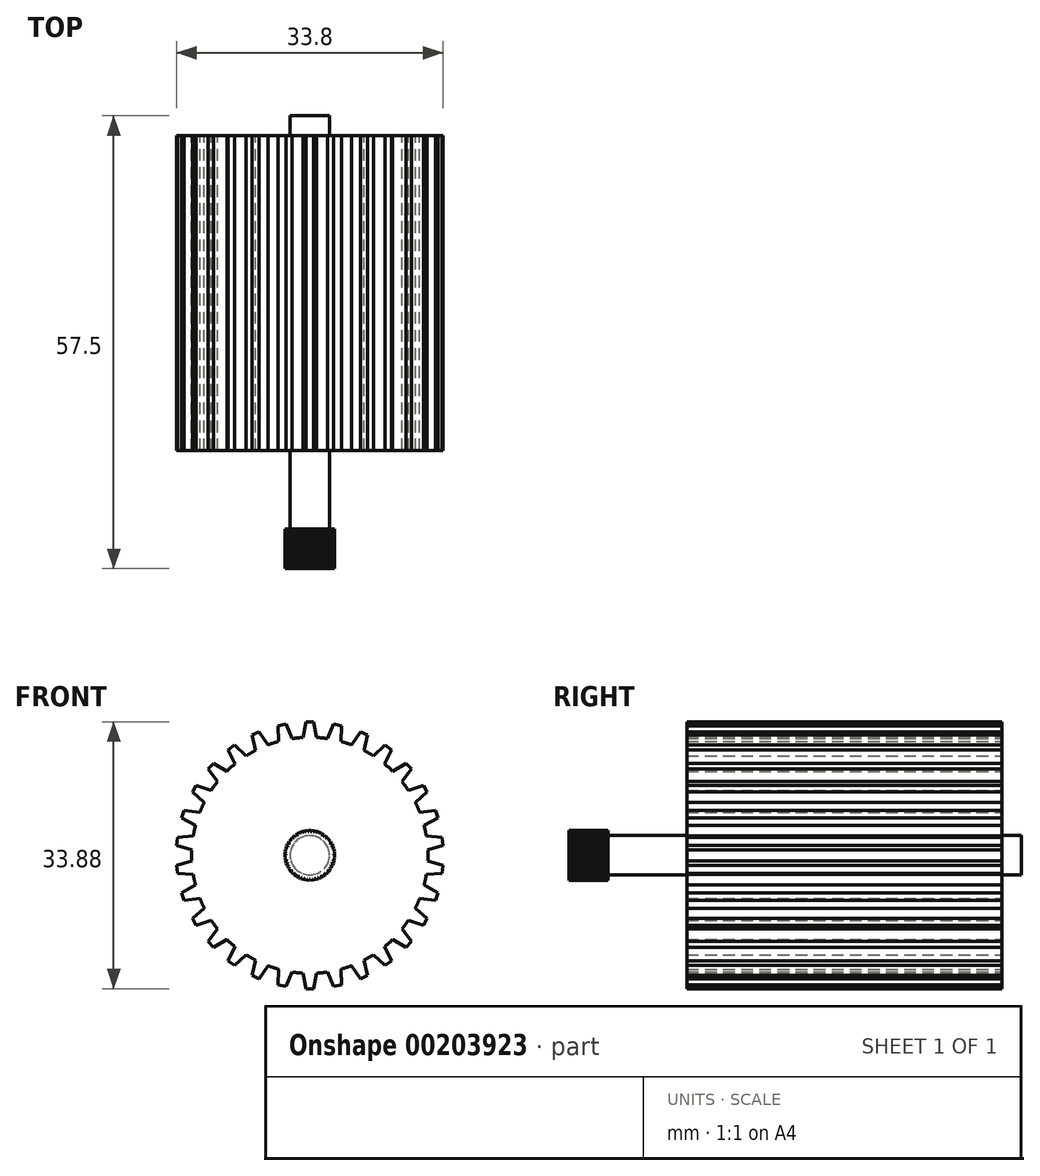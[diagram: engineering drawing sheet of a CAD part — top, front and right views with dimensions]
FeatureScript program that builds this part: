
annotation { "Feature Type Name" : "Feature", "Feature Type Description" : "" }
export const myFeature = defineFeature(function(context is Context, id is Id, definition is map)
    precondition{}
    {
        {
            var Q0;
            Q0=qCreatedBy(makeId("Front.planeOp"),FACE);
            var sketch = newSketch(context, id + "F0", { "sketchPlane" : qUnion([Q0])});
            skCircle(sketch, "E0", {"center": v(0, 0) * mm, "radius": 15 * mm});
            skLineSegment(sketch, "E1", {"start": v(0, 0) * mm, "end": v(0, 16.94) * mm, "construction": true});
            skLineSegment(sketch, "E2", {"start": v(0, 16.94) * mm, "end": v(-0.5, 16.94) * mm});
            skLineSegment(sketch, "E3", {"start": v(-0.5, 16.94) * mm, "end": v(-0.88, 14.97) * mm});
            skLineSegment(sketch, "E4.MirrorCS", {"start": v(0, 16.94) * mm, "end": v(0.5, 16.94) * mm});
            skLineSegment(sketch, "E5.MirrorCS", {"start": v(0.5, 16.94) * mm, "end": v(0.88, 14.97) * mm});
            skLineSegment(sketch, "E6.1.0", {"start": v(-4.01, 16.46) * mm, "end": v(-3.98, 14.46) * mm});
            skLineSegment(sketch, "E6.1.1", {"start": v(-3.52, 16.57) * mm, "end": v(-4.01, 16.46) * mm});
            skLineSegment(sketch, "E6.1.2", {"start": v(-3.52, 16.57) * mm, "end": v(-3.03, 16.67) * mm});
            skLineSegment(sketch, "E6.1.3", {"start": v(-3.03, 16.67) * mm, "end": v(-2.25, 14.83) * mm});
            skLineSegment(sketch, "E6.2.0", {"start": v(-7.35, 15.27) * mm, "end": v(-6.9, 13.32) * mm});
            skLineSegment(sketch, "E6.2.1", {"start": v(-6.89, 15.47) * mm, "end": v(-7.35, 15.27) * mm});
            skLineSegment(sketch, "E6.2.2", {"start": v(-6.89, 15.47) * mm, "end": v(-6.43, 15.68) * mm});
            skLineSegment(sketch, "E6.2.3", {"start": v(-6.43, 15.68) * mm, "end": v(-5.28, 14.04) * mm});
            skLineSegment(sketch, "E7.2.3.0", {"start": v(-10.36, 13.4) * mm, "end": v(-9.52, 11.6) * mm});
            skLineSegment(sketch, "E7.3.3.0", {"start": v(-9.96, 13.7) * mm, "end": v(-10.36, 13.4) * mm});
            skLineSegment(sketch, "E7.6.3.0", {"start": v(-9.96, 13.7) * mm, "end": v(-9.55, 14) * mm});
            skLineSegment(sketch, "E7.9.3.0", {"start": v(-9.55, 14) * mm, "end": v(-8.09, 12.63) * mm});
            skLineSegment(sketch, "E7.2.4.0", {"start": v(-12.92, 10.96) * mm, "end": v(-11.72, 9.36) * mm});
            skLineSegment(sketch, "E7.3.4.0", {"start": v(-12.59, 11.33) * mm, "end": v(-12.92, 10.96) * mm});
            skLineSegment(sketch, "E7.6.4.0", {"start": v(-12.59, 11.33) * mm, "end": v(-12.25, 11.7) * mm});
            skLineSegment(sketch, "E7.9.4.0", {"start": v(-12.25, 11.7) * mm, "end": v(-10.54, 10.68) * mm});
            skLineSegment(sketch, "E7.2.5.0", {"start": v(-14.92, 8.04) * mm, "end": v(-13.4, 6.72) * mm});
            skLineSegment(sketch, "E7.3.5.0", {"start": v(-14.67, 8.47) * mm, "end": v(-14.92, 8.04) * mm});
            skLineSegment(sketch, "E7.6.5.0", {"start": v(-14.67, 8.47) * mm, "end": v(-14.42, 8.9) * mm});
            skLineSegment(sketch, "E7.9.5.0", {"start": v(-14.42, 8.9) * mm, "end": v(-12.53, 8.25) * mm});
            skLineSegment(sketch, "E7.2.6.0", {"start": v(-16.26, 4.76) * mm, "end": v(-14.51, 3.79) * mm});
            skLineSegment(sketch, "E7.3.6.0", {"start": v(-16.1, 5.23) * mm, "end": v(-16.26, 4.76) * mm});
            skLineSegment(sketch, "E7.6.6.0", {"start": v(-16.1, 5.23) * mm, "end": v(-15.95, 5.7) * mm});
            skLineSegment(sketch, "E7.9.6.0", {"start": v(-15.95, 5.7) * mm, "end": v(-13.97, 5.47) * mm});
            skLineSegment(sketch, "E7.2.7.0", {"start": v(-16.9, 1.27) * mm, "end": v(-14.98, 0.69) * mm});
            skLineSegment(sketch, "E7.3.7.0", {"start": v(-16.84, 1.77) * mm, "end": v(-16.9, 1.27) * mm});
            skLineSegment(sketch, "E7.6.7.0", {"start": v(-16.84, 1.77) * mm, "end": v(-16.8, 2.27) * mm});
            skLineSegment(sketch, "E7.9.7.0", {"start": v(-16.8, 2.27) * mm, "end": v(-14.8, 2.44) * mm});
            skLineSegment(sketch, "E7.2.8.0", {"start": v(-16.8, -2.27) * mm, "end": v(-14.8, -2.44) * mm});
            skLineSegment(sketch, "E7.3.8.0", {"start": v(-16.84, -1.77) * mm, "end": v(-16.8, -2.27) * mm});
            skLineSegment(sketch, "E7.6.8.0", {"start": v(-16.84, -1.77) * mm, "end": v(-16.9, -1.27) * mm});
            skLineSegment(sketch, "E7.9.8.0", {"start": v(-16.9, -1.27) * mm, "end": v(-14.98, -0.69) * mm});
            skLineSegment(sketch, "E7.2.9.0", {"start": v(-15.95, -5.7) * mm, "end": v(-13.97, -5.47) * mm});
            skLineSegment(sketch, "E7.3.9.0", {"start": v(-16.1, -5.23) * mm, "end": v(-15.95, -5.7) * mm});
            skLineSegment(sketch, "E7.6.9.0", {"start": v(-16.1, -5.23) * mm, "end": v(-16.26, -4.76) * mm});
            skLineSegment(sketch, "E7.9.9.0", {"start": v(-16.26, -4.76) * mm, "end": v(-14.51, -3.79) * mm});
            skLineSegment(sketch, "E7.2.10.0", {"start": v(-14.42, -8.9) * mm, "end": v(-12.53, -8.25) * mm});
            skLineSegment(sketch, "E7.3.10.0", {"start": v(-14.67, -8.47) * mm, "end": v(-14.42, -8.9) * mm});
            skLineSegment(sketch, "E7.6.10.0", {"start": v(-14.67, -8.47) * mm, "end": v(-14.92, -8.04) * mm});
            skLineSegment(sketch, "E7.9.10.0", {"start": v(-14.92, -8.04) * mm, "end": v(-13.4, -6.72) * mm});
            skLineSegment(sketch, "E7.2.11.0", {"start": v(-12.25, -11.7) * mm, "end": v(-10.54, -10.68) * mm});
            skLineSegment(sketch, "E7.3.11.0", {"start": v(-12.59, -11.33) * mm, "end": v(-12.25, -11.7) * mm});
            skLineSegment(sketch, "E7.6.11.0", {"start": v(-12.59, -11.33) * mm, "end": v(-12.92, -10.96) * mm});
            skLineSegment(sketch, "E7.9.11.0", {"start": v(-12.92, -10.96) * mm, "end": v(-11.72, -9.36) * mm});
            skLineSegment(sketch, "E7.2.12.0", {"start": v(-9.55, -14) * mm, "end": v(-8.09, -12.63) * mm});
            skLineSegment(sketch, "E7.3.12.0", {"start": v(-9.96, -13.7) * mm, "end": v(-9.55, -14) * mm});
            skLineSegment(sketch, "E7.6.12.0", {"start": v(-9.96, -13.7) * mm, "end": v(-10.36, -13.4) * mm});
            skLineSegment(sketch, "E7.9.12.0", {"start": v(-10.36, -13.4) * mm, "end": v(-9.52, -11.6) * mm});
            skLineSegment(sketch, "E7.2.13.0", {"start": v(-6.43, -15.68) * mm, "end": v(-5.28, -14.04) * mm});
            skLineSegment(sketch, "E7.3.13.0", {"start": v(-6.89, -15.47) * mm, "end": v(-6.43, -15.68) * mm});
            skLineSegment(sketch, "E7.6.13.0", {"start": v(-6.89, -15.47) * mm, "end": v(-7.35, -15.27) * mm});
            skLineSegment(sketch, "E7.9.13.0", {"start": v(-7.35, -15.27) * mm, "end": v(-6.9, -13.32) * mm});
            skLineSegment(sketch, "E7.2.14.0", {"start": v(-3.03, -16.67) * mm, "end": v(-2.25, -14.83) * mm});
            skLineSegment(sketch, "E7.3.14.0", {"start": v(-3.52, -16.57) * mm, "end": v(-3.03, -16.67) * mm});
            skLineSegment(sketch, "E7.6.14.0", {"start": v(-3.52, -16.57) * mm, "end": v(-4.01, -16.46) * mm});
            skLineSegment(sketch, "E7.9.14.0", {"start": v(-4.01, -16.46) * mm, "end": v(-3.98, -14.46) * mm});
            skLineSegment(sketch, "E8.2.15.0", {"start": v(0.5, -16.94) * mm, "end": v(0.88, -14.97) * mm});
            skLineSegment(sketch, "E8.3.15.0", {"start": v(0, -16.94) * mm, "end": v(0.5, -16.94) * mm});
            skLineSegment(sketch, "E8.6.15.0", {"start": v(0, -16.94) * mm, "end": v(-0.5, -16.94) * mm});
            skLineSegment(sketch, "E8.9.15.0", {"start": v(-0.5, -16.94) * mm, "end": v(-0.88, -14.97) * mm});
            skLineSegment(sketch, "E8.2.16.0", {"start": v(4.01, -16.46) * mm, "end": v(3.98, -14.46) * mm});
            skLineSegment(sketch, "E8.3.16.0", {"start": v(3.52, -16.57) * mm, "end": v(4.01, -16.46) * mm});
            skLineSegment(sketch, "E8.6.16.0", {"start": v(3.52, -16.57) * mm, "end": v(3.03, -16.67) * mm});
            skLineSegment(sketch, "E8.9.16.0", {"start": v(3.03, -16.67) * mm, "end": v(2.25, -14.83) * mm});
            skLineSegment(sketch, "E8.2.17.0", {"start": v(7.35, -15.27) * mm, "end": v(6.9, -13.32) * mm});
            skLineSegment(sketch, "E8.3.17.0", {"start": v(6.89, -15.47) * mm, "end": v(7.35, -15.27) * mm});
            skLineSegment(sketch, "E8.6.17.0", {"start": v(6.89, -15.47) * mm, "end": v(6.43, -15.68) * mm});
            skLineSegment(sketch, "E8.9.17.0", {"start": v(6.43, -15.68) * mm, "end": v(5.28, -14.04) * mm});
            skLineSegment(sketch, "E8.2.18.0", {"start": v(10.36, -13.4) * mm, "end": v(9.52, -11.6) * mm});
            skLineSegment(sketch, "E8.3.18.0", {"start": v(9.96, -13.7) * mm, "end": v(10.36, -13.4) * mm});
            skLineSegment(sketch, "E8.6.18.0", {"start": v(9.96, -13.7) * mm, "end": v(9.55, -14) * mm});
            skLineSegment(sketch, "E8.9.18.0", {"start": v(9.55, -14) * mm, "end": v(8.09, -12.63) * mm});
            skLineSegment(sketch, "E8.2.19.0", {"start": v(12.92, -10.96) * mm, "end": v(11.72, -9.36) * mm});
            skLineSegment(sketch, "E8.3.19.0", {"start": v(12.59, -11.33) * mm, "end": v(12.92, -10.96) * mm});
            skLineSegment(sketch, "E8.6.19.0", {"start": v(12.59, -11.33) * mm, "end": v(12.25, -11.7) * mm});
            skLineSegment(sketch, "E8.9.19.0", {"start": v(12.25, -11.7) * mm, "end": v(10.54, -10.68) * mm});
            skLineSegment(sketch, "E8.2.20.0", {"start": v(14.92, -8.04) * mm, "end": v(13.4, -6.72) * mm});
            skLineSegment(sketch, "E8.3.20.0", {"start": v(14.67, -8.47) * mm, "end": v(14.92, -8.04) * mm});
            skLineSegment(sketch, "E8.6.20.0", {"start": v(14.67, -8.47) * mm, "end": v(14.42, -8.9) * mm});
            skLineSegment(sketch, "E8.9.20.0", {"start": v(14.42, -8.9) * mm, "end": v(12.53, -8.25) * mm});
            skLineSegment(sketch, "E8.2.21.0", {"start": v(16.26, -4.76) * mm, "end": v(14.51, -3.79) * mm});
            skLineSegment(sketch, "E8.3.21.0", {"start": v(16.1, -5.23) * mm, "end": v(16.26, -4.76) * mm});
            skLineSegment(sketch, "E8.6.21.0", {"start": v(16.1, -5.23) * mm, "end": v(15.95, -5.7) * mm});
            skLineSegment(sketch, "E8.9.21.0", {"start": v(15.95, -5.7) * mm, "end": v(13.97, -5.47) * mm});
            skLineSegment(sketch, "E8.2.22.0", {"start": v(16.9, -1.27) * mm, "end": v(14.98, -0.69) * mm});
            skLineSegment(sketch, "E8.3.22.0", {"start": v(16.84, -1.77) * mm, "end": v(16.9, -1.27) * mm});
            skLineSegment(sketch, "E8.6.22.0", {"start": v(16.84, -1.77) * mm, "end": v(16.8, -2.27) * mm});
            skLineSegment(sketch, "E8.9.22.0", {"start": v(16.8, -2.27) * mm, "end": v(14.8, -2.44) * mm});
            skLineSegment(sketch, "E8.2.23.0", {"start": v(16.8, 2.27) * mm, "end": v(14.8, 2.44) * mm});
            skLineSegment(sketch, "E8.3.23.0", {"start": v(16.84, 1.77) * mm, "end": v(16.8, 2.27) * mm});
            skLineSegment(sketch, "E8.6.23.0", {"start": v(16.84, 1.77) * mm, "end": v(16.9, 1.27) * mm});
            skLineSegment(sketch, "E8.9.23.0", {"start": v(16.9, 1.27) * mm, "end": v(14.98, 0.69) * mm});
            skLineSegment(sketch, "E8.2.24.0", {"start": v(15.95, 5.7) * mm, "end": v(13.97, 5.47) * mm});
            skLineSegment(sketch, "E8.3.24.0", {"start": v(16.1, 5.23) * mm, "end": v(15.95, 5.7) * mm});
            skLineSegment(sketch, "E8.6.24.0", {"start": v(16.1, 5.23) * mm, "end": v(16.26, 4.76) * mm});
            skLineSegment(sketch, "E8.9.24.0", {"start": v(16.26, 4.76) * mm, "end": v(14.51, 3.79) * mm});
            skLineSegment(sketch, "E9.2.25.0", {"start": v(14.42, 8.9) * mm, "end": v(12.53, 8.25) * mm});
            skLineSegment(sketch, "E9.3.25.0", {"start": v(14.67, 8.47) * mm, "end": v(14.42, 8.9) * mm});
            skLineSegment(sketch, "E9.6.25.0", {"start": v(14.67, 8.47) * mm, "end": v(14.92, 8.04) * mm});
            skLineSegment(sketch, "E9.9.25.0", {"start": v(14.92, 8.04) * mm, "end": v(13.4, 6.72) * mm});
            skLineSegment(sketch, "E9.2.26.0", {"start": v(12.25, 11.7) * mm, "end": v(10.54, 10.68) * mm});
            skLineSegment(sketch, "E9.3.26.0", {"start": v(12.59, 11.33) * mm, "end": v(12.25, 11.7) * mm});
            skLineSegment(sketch, "E9.6.26.0", {"start": v(12.59, 11.33) * mm, "end": v(12.92, 10.96) * mm});
            skLineSegment(sketch, "E9.9.26.0", {"start": v(12.92, 10.96) * mm, "end": v(11.72, 9.36) * mm});
            skLineSegment(sketch, "E9.2.27.0", {"start": v(9.55, 14) * mm, "end": v(8.09, 12.63) * mm});
            skLineSegment(sketch, "E9.3.27.0", {"start": v(9.96, 13.7) * mm, "end": v(9.55, 14) * mm});
            skLineSegment(sketch, "E9.6.27.0", {"start": v(9.96, 13.7) * mm, "end": v(10.36, 13.4) * mm});
            skLineSegment(sketch, "E9.9.27.0", {"start": v(10.36, 13.4) * mm, "end": v(9.52, 11.6) * mm});
            skLineSegment(sketch, "E9.2.28.0", {"start": v(6.43, 15.68) * mm, "end": v(5.28, 14.04) * mm});
            skLineSegment(sketch, "E9.3.28.0", {"start": v(6.89, 15.47) * mm, "end": v(6.43, 15.68) * mm});
            skLineSegment(sketch, "E9.6.28.0", {"start": v(6.89, 15.47) * mm, "end": v(7.35, 15.27) * mm});
            skLineSegment(sketch, "E9.9.28.0", {"start": v(7.35, 15.27) * mm, "end": v(6.9, 13.32) * mm});
            skLineSegment(sketch, "E9.2.29.0", {"start": v(3.03, 16.67) * mm, "end": v(2.25, 14.83) * mm});
            skLineSegment(sketch, "E9.3.29.0", {"start": v(3.52, 16.57) * mm, "end": v(3.03, 16.67) * mm});
            skLineSegment(sketch, "E9.6.29.0", {"start": v(3.52, 16.57) * mm, "end": v(4.01, 16.46) * mm});
            skLineSegment(sketch, "E9.9.29.0", {"start": v(4.01, 16.46) * mm, "end": v(3.98, 14.46) * mm});
            skSolve(sketch);
        }
        {
            var Q0;
            Q0=qSketchRegion(id+"F0",true);
            extrude(context, id + "F1", {"entities" : qUnion([Q0]), "depth" : 40 * mm});
        }
        {
            var Q0;
            Q0=makeQuery(id+"F1.opExtrude","CAP_FACE",FACE,{"disambiguationData":[OSD([sQuery(id+"F0.wireOp",EDGE,"E0"),sQuery(id+"F0.wireOp",EDGE,"E2"),sQuery(id+"F0.wireOp",EDGE,"E3"),sQuery(id+"F0.wireOp",EDGE,"E4.MirrorCS"),sQuery(id+"F0.wireOp",EDGE,"E5.MirrorCS"),sQuery(id+"F0.wireOp",EDGE,"E6.1.0"),sQuery(id+"F0.wireOp",EDGE,"E6.1.1"),sQuery(id+"F0.wireOp",EDGE,"E6.1.2"),sQuery(id+"F0.wireOp",EDGE,"E6.1.3"),sQuery(id+"F0.wireOp",EDGE,"E6.2.0"),sQuery(id+"F0.wireOp",EDGE,"E6.2.1"),sQuery(id+"F0.wireOp",EDGE,"E6.2.2"),sQuery(id+"F0.wireOp",EDGE,"E6.2.3"),sQuery(id+"F0.wireOp",EDGE,"E7.2.3.0"),sQuery(id+"F0.wireOp",EDGE,"E7.3.3.0"),sQuery(id+"F0.wireOp",EDGE,"E7.6.3.0"),sQuery(id+"F0.wireOp",EDGE,"E7.9.3.0"),sQuery(id+"F0.wireOp",EDGE,"E7.2.4.0"),sQuery(id+"F0.wireOp",EDGE,"E7.3.4.0"),sQuery(id+"F0.wireOp",EDGE,"E7.6.4.0"),sQuery(id+"F0.wireOp",EDGE,"E7.9.4.0"),sQuery(id+"F0.wireOp",EDGE,"E7.2.5.0"),sQuery(id+"F0.wireOp",EDGE,"E7.3.5.0"),sQuery(id+"F0.wireOp",EDGE,"E7.6.5.0"),sQuery(id+"F0.wireOp",EDGE,"E7.9.5.0"),sQuery(id+"F0.wireOp",EDGE,"E7.2.6.0"),sQuery(id+"F0.wireOp",EDGE,"E7.3.6.0"),sQuery(id+"F0.wireOp",EDGE,"E7.6.6.0"),sQuery(id+"F0.wireOp",EDGE,"E7.9.6.0"),sQuery(id+"F0.wireOp",EDGE,"E7.2.7.0"),sQuery(id+"F0.wireOp",EDGE,"E7.3.7.0"),sQuery(id+"F0.wireOp",EDGE,"E7.6.7.0"),sQuery(id+"F0.wireOp",EDGE,"E7.9.7.0"),sQuery(id+"F0.wireOp",EDGE,"E7.2.8.0"),sQuery(id+"F0.wireOp",EDGE,"E7.3.8.0"),sQuery(id+"F0.wireOp",EDGE,"E7.6.8.0"),sQuery(id+"F0.wireOp",EDGE,"E7.9.8.0"),sQuery(id+"F0.wireOp",EDGE,"E7.2.9.0"),sQuery(id+"F0.wireOp",EDGE,"E7.3.9.0"),sQuery(id+"F0.wireOp",EDGE,"E7.6.9.0"),sQuery(id+"F0.wireOp",EDGE,"E7.9.9.0"),sQuery(id+"F0.wireOp",EDGE,"E7.2.10.0"),sQuery(id+"F0.wireOp",EDGE,"E7.3.10.0"),sQuery(id+"F0.wireOp",EDGE,"E7.6.10.0"),sQuery(id+"F0.wireOp",EDGE,"E7.9.10.0"),sQuery(id+"F0.wireOp",EDGE,"E7.2.11.0"),sQuery(id+"F0.wireOp",EDGE,"E7.3.11.0"),sQuery(id+"F0.wireOp",EDGE,"E7.6.11.0"),sQuery(id+"F0.wireOp",EDGE,"E7.9.11.0"),sQuery(id+"F0.wireOp",EDGE,"E7.2.12.0"),sQuery(id+"F0.wireOp",EDGE,"E7.3.12.0"),sQuery(id+"F0.wireOp",EDGE,"E7.6.12.0"),sQuery(id+"F0.wireOp",EDGE,"E7.9.12.0"),sQuery(id+"F0.wireOp",EDGE,"E7.2.13.0"),sQuery(id+"F0.wireOp",EDGE,"E7.3.13.0"),sQuery(id+"F0.wireOp",EDGE,"E7.6.13.0"),sQuery(id+"F0.wireOp",EDGE,"E7.9.13.0"),sQuery(id+"F0.wireOp",EDGE,"E7.2.14.0"),sQuery(id+"F0.wireOp",EDGE,"E7.3.14.0"),sQuery(id+"F0.wireOp",EDGE,"E7.6.14.0"),sQuery(id+"F0.wireOp",EDGE,"E7.9.14.0"),sQuery(id+"F0.wireOp",EDGE,"E8.2.15.0"),sQuery(id+"F0.wireOp",EDGE,"E8.3.15.0"),sQuery(id+"F0.wireOp",EDGE,"E8.6.15.0"),sQuery(id+"F0.wireOp",EDGE,"E8.9.15.0"),sQuery(id+"F0.wireOp",EDGE,"E8.2.16.0"),sQuery(id+"F0.wireOp",EDGE,"E8.3.16.0"),sQuery(id+"F0.wireOp",EDGE,"E8.6.16.0"),sQuery(id+"F0.wireOp",EDGE,"E8.9.16.0"),sQuery(id+"F0.wireOp",EDGE,"E8.2.17.0"),sQuery(id+"F0.wireOp",EDGE,"E8.3.17.0"),sQuery(id+"F0.wireOp",EDGE,"E8.6.17.0"),sQuery(id+"F0.wireOp",EDGE,"E8.9.17.0"),sQuery(id+"F0.wireOp",EDGE,"E8.2.18.0"),sQuery(id+"F0.wireOp",EDGE,"E8.3.18.0"),sQuery(id+"F0.wireOp",EDGE,"E8.6.18.0"),sQuery(id+"F0.wireOp",EDGE,"E8.9.18.0"),sQuery(id+"F0.wireOp",EDGE,"E8.2.19.0"),sQuery(id+"F0.wireOp",EDGE,"E8.3.19.0"),sQuery(id+"F0.wireOp",EDGE,"E8.6.19.0"),sQuery(id+"F0.wireOp",EDGE,"E8.9.19.0"),sQuery(id+"F0.wireOp",EDGE,"E8.2.20.0"),sQuery(id+"F0.wireOp",EDGE,"E8.3.20.0"),sQuery(id+"F0.wireOp",EDGE,"E8.6.20.0"),sQuery(id+"F0.wireOp",EDGE,"E8.9.20.0"),sQuery(id+"F0.wireOp",EDGE,"E8.2.21.0"),sQuery(id+"F0.wireOp",EDGE,"E8.3.21.0"),sQuery(id+"F0.wireOp",EDGE,"E8.6.21.0"),sQuery(id+"F0.wireOp",EDGE,"E8.9.21.0"),sQuery(id+"F0.wireOp",EDGE,"E8.2.22.0"),sQuery(id+"F0.wireOp",EDGE,"E8.3.22.0"),sQuery(id+"F0.wireOp",EDGE,"E8.6.22.0"),sQuery(id+"F0.wireOp",EDGE,"E8.9.22.0"),sQuery(id+"F0.wireOp",EDGE,"E8.2.23.0"),sQuery(id+"F0.wireOp",EDGE,"E8.3.23.0"),sQuery(id+"F0.wireOp",EDGE,"E8.6.23.0"),sQuery(id+"F0.wireOp",EDGE,"E8.9.23.0"),sQuery(id+"F0.wireOp",EDGE,"E8.2.24.0"),sQuery(id+"F0.wireOp",EDGE,"E8.3.24.0"),sQuery(id+"F0.wireOp",EDGE,"E8.6.24.0"),sQuery(id+"F0.wireOp",EDGE,"E8.9.24.0"),sQuery(id+"F0.wireOp",EDGE,"E9.2.25.0"),sQuery(id+"F0.wireOp",EDGE,"E9.3.25.0"),sQuery(id+"F0.wireOp",EDGE,"E9.6.25.0"),sQuery(id+"F0.wireOp",EDGE,"E9.9.25.0"),sQuery(id+"F0.wireOp",EDGE,"E9.2.26.0"),sQuery(id+"F0.wireOp",EDGE,"E9.3.26.0"),sQuery(id+"F0.wireOp",EDGE,"E9.6.26.0"),sQuery(id+"F0.wireOp",EDGE,"E9.9.26.0"),sQuery(id+"F0.wireOp",EDGE,"E9.2.27.0"),sQuery(id+"F0.wireOp",EDGE,"E9.3.27.0"),sQuery(id+"F0.wireOp",EDGE,"E9.6.27.0"),sQuery(id+"F0.wireOp",EDGE,"E9.9.27.0"),sQuery(id+"F0.wireOp",EDGE,"E9.2.28.0"),sQuery(id+"F0.wireOp",EDGE,"E9.3.28.0"),sQuery(id+"F0.wireOp",EDGE,"E9.6.28.0"),sQuery(id+"F0.wireOp",EDGE,"E9.9.28.0"),sQuery(id+"F0.wireOp",EDGE,"E9.2.29.0"),sQuery(id+"F0.wireOp",EDGE,"E9.3.29.0"),sQuery(id+"F0.wireOp",EDGE,"E9.6.29.0"),sQuery(id+"F0.wireOp",EDGE,"E9.9.29.0")])],"isStart":false});
            var sketch = newSketch(context, id + "F2", { "sketchPlane" : qUnion([Q0])});
            skCircle(sketch, "E10", {"center": v(0, 0) * mm, "radius": 2.5 * mm});
            skSolve(sketch);
        }
        {
            var Q0;
            Q0=qSketchRegion(id+"F2",true);
            extrude(context, id + "F3", {"entities" : qUnion([Q0]), "operationType" : NewBodyOperationType.ADD, "depth" : 15 * mm});
        }
        {
            var Q0;
            Q0=makeQuery(id+"F1.opExtrude","CAP_FACE",FACE,{"disambiguationData":[OSD([sQuery(id+"F0.wireOp",EDGE,"E0"),sQuery(id+"F0.wireOp",EDGE,"E2"),sQuery(id+"F0.wireOp",EDGE,"E3"),sQuery(id+"F0.wireOp",EDGE,"E4.MirrorCS"),sQuery(id+"F0.wireOp",EDGE,"E5.MirrorCS"),sQuery(id+"F0.wireOp",EDGE,"E6.1.0"),sQuery(id+"F0.wireOp",EDGE,"E6.1.1"),sQuery(id+"F0.wireOp",EDGE,"E6.1.2"),sQuery(id+"F0.wireOp",EDGE,"E6.1.3"),sQuery(id+"F0.wireOp",EDGE,"E6.2.0"),sQuery(id+"F0.wireOp",EDGE,"E6.2.1"),sQuery(id+"F0.wireOp",EDGE,"E6.2.2"),sQuery(id+"F0.wireOp",EDGE,"E6.2.3"),sQuery(id+"F0.wireOp",EDGE,"E7.2.3.0"),sQuery(id+"F0.wireOp",EDGE,"E7.3.3.0"),sQuery(id+"F0.wireOp",EDGE,"E7.6.3.0"),sQuery(id+"F0.wireOp",EDGE,"E7.9.3.0"),sQuery(id+"F0.wireOp",EDGE,"E7.2.4.0"),sQuery(id+"F0.wireOp",EDGE,"E7.3.4.0"),sQuery(id+"F0.wireOp",EDGE,"E7.6.4.0"),sQuery(id+"F0.wireOp",EDGE,"E7.9.4.0"),sQuery(id+"F0.wireOp",EDGE,"E7.2.5.0"),sQuery(id+"F0.wireOp",EDGE,"E7.3.5.0"),sQuery(id+"F0.wireOp",EDGE,"E7.6.5.0"),sQuery(id+"F0.wireOp",EDGE,"E7.9.5.0"),sQuery(id+"F0.wireOp",EDGE,"E7.2.6.0"),sQuery(id+"F0.wireOp",EDGE,"E7.3.6.0"),sQuery(id+"F0.wireOp",EDGE,"E7.6.6.0"),sQuery(id+"F0.wireOp",EDGE,"E7.9.6.0"),sQuery(id+"F0.wireOp",EDGE,"E7.2.7.0"),sQuery(id+"F0.wireOp",EDGE,"E7.3.7.0"),sQuery(id+"F0.wireOp",EDGE,"E7.6.7.0"),sQuery(id+"F0.wireOp",EDGE,"E7.9.7.0"),sQuery(id+"F0.wireOp",EDGE,"E7.2.8.0"),sQuery(id+"F0.wireOp",EDGE,"E7.3.8.0"),sQuery(id+"F0.wireOp",EDGE,"E7.6.8.0"),sQuery(id+"F0.wireOp",EDGE,"E7.9.8.0"),sQuery(id+"F0.wireOp",EDGE,"E7.2.9.0"),sQuery(id+"F0.wireOp",EDGE,"E7.3.9.0"),sQuery(id+"F0.wireOp",EDGE,"E7.6.9.0"),sQuery(id+"F0.wireOp",EDGE,"E7.9.9.0"),sQuery(id+"F0.wireOp",EDGE,"E7.2.10.0"),sQuery(id+"F0.wireOp",EDGE,"E7.3.10.0"),sQuery(id+"F0.wireOp",EDGE,"E7.6.10.0"),sQuery(id+"F0.wireOp",EDGE,"E7.9.10.0"),sQuery(id+"F0.wireOp",EDGE,"E7.2.11.0"),sQuery(id+"F0.wireOp",EDGE,"E7.3.11.0"),sQuery(id+"F0.wireOp",EDGE,"E7.6.11.0"),sQuery(id+"F0.wireOp",EDGE,"E7.9.11.0"),sQuery(id+"F0.wireOp",EDGE,"E7.2.12.0"),sQuery(id+"F0.wireOp",EDGE,"E7.3.12.0"),sQuery(id+"F0.wireOp",EDGE,"E7.6.12.0"),sQuery(id+"F0.wireOp",EDGE,"E7.9.12.0"),sQuery(id+"F0.wireOp",EDGE,"E7.2.13.0"),sQuery(id+"F0.wireOp",EDGE,"E7.3.13.0"),sQuery(id+"F0.wireOp",EDGE,"E7.6.13.0"),sQuery(id+"F0.wireOp",EDGE,"E7.9.13.0"),sQuery(id+"F0.wireOp",EDGE,"E7.2.14.0"),sQuery(id+"F0.wireOp",EDGE,"E7.3.14.0"),sQuery(id+"F0.wireOp",EDGE,"E7.6.14.0"),sQuery(id+"F0.wireOp",EDGE,"E7.9.14.0"),sQuery(id+"F0.wireOp",EDGE,"E8.2.15.0"),sQuery(id+"F0.wireOp",EDGE,"E8.3.15.0"),sQuery(id+"F0.wireOp",EDGE,"E8.6.15.0"),sQuery(id+"F0.wireOp",EDGE,"E8.9.15.0"),sQuery(id+"F0.wireOp",EDGE,"E8.2.16.0"),sQuery(id+"F0.wireOp",EDGE,"E8.3.16.0"),sQuery(id+"F0.wireOp",EDGE,"E8.6.16.0"),sQuery(id+"F0.wireOp",EDGE,"E8.9.16.0"),sQuery(id+"F0.wireOp",EDGE,"E8.2.17.0"),sQuery(id+"F0.wireOp",EDGE,"E8.3.17.0"),sQuery(id+"F0.wireOp",EDGE,"E8.6.17.0"),sQuery(id+"F0.wireOp",EDGE,"E8.9.17.0"),sQuery(id+"F0.wireOp",EDGE,"E8.2.18.0"),sQuery(id+"F0.wireOp",EDGE,"E8.3.18.0"),sQuery(id+"F0.wireOp",EDGE,"E8.6.18.0"),sQuery(id+"F0.wireOp",EDGE,"E8.9.18.0"),sQuery(id+"F0.wireOp",EDGE,"E8.2.19.0"),sQuery(id+"F0.wireOp",EDGE,"E8.3.19.0"),sQuery(id+"F0.wireOp",EDGE,"E8.6.19.0"),sQuery(id+"F0.wireOp",EDGE,"E8.9.19.0"),sQuery(id+"F0.wireOp",EDGE,"E8.2.20.0"),sQuery(id+"F0.wireOp",EDGE,"E8.3.20.0"),sQuery(id+"F0.wireOp",EDGE,"E8.6.20.0"),sQuery(id+"F0.wireOp",EDGE,"E8.9.20.0"),sQuery(id+"F0.wireOp",EDGE,"E8.2.21.0"),sQuery(id+"F0.wireOp",EDGE,"E8.3.21.0"),sQuery(id+"F0.wireOp",EDGE,"E8.6.21.0"),sQuery(id+"F0.wireOp",EDGE,"E8.9.21.0"),sQuery(id+"F0.wireOp",EDGE,"E8.2.22.0"),sQuery(id+"F0.wireOp",EDGE,"E8.3.22.0"),sQuery(id+"F0.wireOp",EDGE,"E8.6.22.0"),sQuery(id+"F0.wireOp",EDGE,"E8.9.22.0"),sQuery(id+"F0.wireOp",EDGE,"E8.2.23.0"),sQuery(id+"F0.wireOp",EDGE,"E8.3.23.0"),sQuery(id+"F0.wireOp",EDGE,"E8.6.23.0"),sQuery(id+"F0.wireOp",EDGE,"E8.9.23.0"),sQuery(id+"F0.wireOp",EDGE,"E8.2.24.0"),sQuery(id+"F0.wireOp",EDGE,"E8.3.24.0"),sQuery(id+"F0.wireOp",EDGE,"E8.6.24.0"),sQuery(id+"F0.wireOp",EDGE,"E8.9.24.0"),sQuery(id+"F0.wireOp",EDGE,"E9.2.25.0"),sQuery(id+"F0.wireOp",EDGE,"E9.3.25.0"),sQuery(id+"F0.wireOp",EDGE,"E9.6.25.0"),sQuery(id+"F0.wireOp",EDGE,"E9.9.25.0"),sQuery(id+"F0.wireOp",EDGE,"E9.2.26.0"),sQuery(id+"F0.wireOp",EDGE,"E9.3.26.0"),sQuery(id+"F0.wireOp",EDGE,"E9.6.26.0"),sQuery(id+"F0.wireOp",EDGE,"E9.9.26.0"),sQuery(id+"F0.wireOp",EDGE,"E9.2.27.0"),sQuery(id+"F0.wireOp",EDGE,"E9.3.27.0"),sQuery(id+"F0.wireOp",EDGE,"E9.6.27.0"),sQuery(id+"F0.wireOp",EDGE,"E9.9.27.0"),sQuery(id+"F0.wireOp",EDGE,"E9.2.28.0"),sQuery(id+"F0.wireOp",EDGE,"E9.3.28.0"),sQuery(id+"F0.wireOp",EDGE,"E9.6.28.0"),sQuery(id+"F0.wireOp",EDGE,"E9.9.28.0"),sQuery(id+"F0.wireOp",EDGE,"E9.2.29.0"),sQuery(id+"F0.wireOp",EDGE,"E9.3.29.0"),sQuery(id+"F0.wireOp",EDGE,"E9.6.29.0"),sQuery(id+"F0.wireOp",EDGE,"E9.9.29.0")])],"isStart":true});
            var sketch = newSketch(context, id + "F4", { "sketchPlane" : qUnion([Q0])});
            skCircle(sketch, "E11", {"center": v(0, 0) * mm, "radius": 2.5 * mm});
            skSolve(sketch);
        }
        {
            var Q0;
            Q0=qSketchRegion(id+"F4",true);
            extrude(context, id + "F5", {"entities" : qUnion([Q0]), "operationType" : NewBodyOperationType.ADD, "depth" : 2.5 * mm});
        }
        {
            var Q0;
            Q0=makeQuery(id+"F3.opExtrude","CAP_FACE",FACE,{"disambiguationData":[OSD([sQuery(id+"F2.wireOp",EDGE,"E10")])],"isStart":false});
            var sketch = newSketch(context, id + "F6", { "sketchPlane" : qUnion([Q0])});
            skCircle(sketch, "E12", {"center": v(0, 0) * mm, "radius": 3 * mm});
            skLineSegment(sketch, "E13", {"start": v(0, 0) * mm, "end": v(0, 5.06) * mm, "construction": true});
            skLineSegment(sketch, "E14.bottom", {"start": v(0.15, 3.15) * mm, "end": v(-0.15, 3.15) * mm});
            skLineSegment(sketch, "E14.top", {"start": v(0.15, 2.85) * mm, "end": v(-0.15, 2.85) * mm});
            skLineSegment(sketch, "E14.left", {"start": v(0.15, 3.15) * mm, "end": v(0.15, 2.85) * mm});
            skLineSegment(sketch, "E14.right", {"start": v(-0.15, 3.15) * mm, "end": v(-0.15, 2.85) * mm});
            skPoint(sketch, "E14.middle", {"position": v(0, 3) * mm});
            skLineSegment(sketch, "E15.1.0", {"start": v(-0.21, 3.15) * mm, "end": v(-0.18, 2.85) * mm});
            skLineSegment(sketch, "E15.1.1", {"start": v(-0.21, 3.15) * mm, "end": v(-0.5, 3.11) * mm});
            skLineSegment(sketch, "E15.1.2", {"start": v(-0.5, 3.11) * mm, "end": v(-0.47, 2.81) * mm});
            skLineSegment(sketch, "E15.1.3", {"start": v(-0.18, 2.85) * mm, "end": v(-0.47, 2.81) * mm});
            skLineSegment(sketch, "E15.2.0", {"start": v(-0.57, 3.1) * mm, "end": v(-0.5, 2.8) * mm});
            skLineSegment(sketch, "E15.2.1", {"start": v(-0.57, 3.1) * mm, "end": v(-0.86, 3.03) * mm});
            skLineSegment(sketch, "E15.2.2", {"start": v(-0.86, 3.03) * mm, "end": v(-0.8, 2.74) * mm});
            skLineSegment(sketch, "E15.2.3", {"start": v(-0.5, 2.8) * mm, "end": v(-0.8, 2.74) * mm});
            skLineSegment(sketch, "E16.2.3.0", {"start": v(-0.92, 3.02) * mm, "end": v(-0.82, 2.73) * mm});
            skLineSegment(sketch, "E16.3.3.0", {"start": v(-0.92, 3.02) * mm, "end": v(-1.2, 2.92) * mm});
            skLineSegment(sketch, "E16.6.3.0", {"start": v(-1.2, 2.92) * mm, "end": v(-1.1, 2.63) * mm});
            skLineSegment(sketch, "E16.9.3.0", {"start": v(-0.82, 2.73) * mm, "end": v(-1.1, 2.63) * mm});
            skLineSegment(sketch, "E16.2.4.0", {"start": v(-1.26, 2.9) * mm, "end": v(-1.12, 2.62) * mm});
            skLineSegment(sketch, "E16.3.4.0", {"start": v(-1.26, 2.9) * mm, "end": v(-1.52, 2.76) * mm});
            skLineSegment(sketch, "E16.6.4.0", {"start": v(-1.52, 2.76) * mm, "end": v(-1.4, 2.5) * mm});
            skLineSegment(sketch, "E16.9.4.0", {"start": v(-1.12, 2.62) * mm, "end": v(-1.4, 2.5) * mm});
            skLineSegment(sketch, "E16.2.5.0", {"start": v(-1.58, 2.73) * mm, "end": v(-1.41, 2.48) * mm});
            skLineSegment(sketch, "E16.3.5.0", {"start": v(-1.58, 2.73) * mm, "end": v(-1.83, 2.57) * mm});
            skLineSegment(sketch, "E16.6.5.0", {"start": v(-1.83, 2.57) * mm, "end": v(-1.67, 2.32) * mm});
            skLineSegment(sketch, "E16.9.5.0", {"start": v(-1.41, 2.48) * mm, "end": v(-1.67, 2.32) * mm});
            skLineSegment(sketch, "E16.2.6.0", {"start": v(-1.88, 2.53) * mm, "end": v(-1.69, 2.3) * mm});
            skLineSegment(sketch, "E16.3.6.0", {"start": v(-1.88, 2.53) * mm, "end": v(-2.11, 2.34) * mm});
            skLineSegment(sketch, "E16.6.6.0", {"start": v(-2.11, 2.34) * mm, "end": v(-1.92, 2.11) * mm});
            skLineSegment(sketch, "E16.9.6.0", {"start": v(-1.69, 2.3) * mm, "end": v(-1.92, 2.11) * mm});
            skLineSegment(sketch, "E16.2.7.0", {"start": v(-2.15, 2.3) * mm, "end": v(-1.94, 2.1) * mm});
            skLineSegment(sketch, "E16.3.7.0", {"start": v(-2.15, 2.3) * mm, "end": v(-2.36, 2.09) * mm});
            skLineSegment(sketch, "E16.6.7.0", {"start": v(-2.36, 2.09) * mm, "end": v(-2.15, 1.88) * mm});
            skLineSegment(sketch, "E16.9.7.0", {"start": v(-1.94, 2.1) * mm, "end": v(-2.15, 1.88) * mm});
            skLineSegment(sketch, "E16.2.8.0", {"start": v(-2.4, 2.04) * mm, "end": v(-2.17, 1.86) * mm});
            skLineSegment(sketch, "E16.3.8.0", {"start": v(-2.4, 2.04) * mm, "end": v(-2.59, 1.8) * mm});
            skLineSegment(sketch, "E16.6.8.0", {"start": v(-2.59, 1.8) * mm, "end": v(-2.35, 1.62) * mm});
            skLineSegment(sketch, "E16.9.8.0", {"start": v(-2.17, 1.86) * mm, "end": v(-2.35, 1.62) * mm});
            skLineSegment(sketch, "E16.2.9.0", {"start": v(-2.62, 1.76) * mm, "end": v(-2.36, 1.6) * mm});
            skLineSegment(sketch, "E16.3.9.0", {"start": v(-2.62, 1.76) * mm, "end": v(-2.77, 1.5) * mm});
            skLineSegment(sketch, "E16.6.9.0", {"start": v(-2.77, 1.5) * mm, "end": v(-2.52, 1.34) * mm});
            skLineSegment(sketch, "E16.9.9.0", {"start": v(-2.36, 1.6) * mm, "end": v(-2.52, 1.34) * mm});
            skLineSegment(sketch, "E17.2.10.0", {"start": v(-2.8, 1.45) * mm, "end": v(-2.53, 1.32) * mm});
            skLineSegment(sketch, "E17.3.10.0", {"start": v(-2.8, 1.45) * mm, "end": v(-2.93, 1.17) * mm});
            skLineSegment(sketch, "E17.6.10.0", {"start": v(-2.93, 1.17) * mm, "end": v(-2.65, 1.05) * mm});
            skLineSegment(sketch, "E17.9.10.0", {"start": v(-2.53, 1.32) * mm, "end": v(-2.65, 1.05) * mm});
            skLineSegment(sketch, "E17.2.11.0", {"start": v(-2.95, 1.12) * mm, "end": v(-2.66, 1.02) * mm});
            skLineSegment(sketch, "E17.3.11.0", {"start": v(-2.95, 1.12) * mm, "end": v(-3.04, 0.83) * mm});
            skLineSegment(sketch, "E17.6.11.0", {"start": v(-3.04, 0.83) * mm, "end": v(-2.76, 0.74) * mm});
            skLineSegment(sketch, "E17.9.11.0", {"start": v(-2.66, 1.02) * mm, "end": v(-2.76, 0.74) * mm});
            skLineSegment(sketch, "E17.2.12.0", {"start": v(-3.06, 0.77) * mm, "end": v(-2.76, 0.71) * mm});
            skLineSegment(sketch, "E17.3.12.0", {"start": v(-3.06, 0.77) * mm, "end": v(-3.12, 0.48) * mm});
            skLineSegment(sketch, "E17.6.12.0", {"start": v(-3.12, 0.48) * mm, "end": v(-2.82, 0.42) * mm});
            skLineSegment(sketch, "E17.9.12.0", {"start": v(-2.76, 0.71) * mm, "end": v(-2.82, 0.42) * mm});
            skLineSegment(sketch, "E17.2.13.0", {"start": v(-3.13, 0.42) * mm, "end": v(-2.83, 0.4) * mm});
            skLineSegment(sketch, "E17.3.13.0", {"start": v(-3.13, 0.42) * mm, "end": v(-3.15, 0.12) * mm});
            skLineSegment(sketch, "E17.6.13.0", {"start": v(-3.15, 0.12) * mm, "end": v(-2.85, 0.1) * mm});
            skLineSegment(sketch, "E17.9.13.0", {"start": v(-2.83, 0.4) * mm, "end": v(-2.85, 0.1) * mm});
            skLineSegment(sketch, "E17.2.14.0", {"start": v(-3.15, 0.06) * mm, "end": v(-2.85, 0.07) * mm});
            skLineSegment(sketch, "E17.3.14.0", {"start": v(-3.15, 0.06) * mm, "end": v(-3.14, -0.24) * mm});
            skLineSegment(sketch, "E17.6.14.0", {"start": v(-3.14, -0.24) * mm, "end": v(-2.84, -0.23) * mm});
            skLineSegment(sketch, "E17.9.14.0", {"start": v(-2.85, 0.07) * mm, "end": v(-2.84, -0.23) * mm});
            skLineSegment(sketch, "E17.2.15.0", {"start": v(-3.14, -0.3) * mm, "end": v(-2.84, -0.26) * mm});
            skLineSegment(sketch, "E17.3.15.0", {"start": v(-3.14, -0.3) * mm, "end": v(-3.1, -0.6) * mm});
            skLineSegment(sketch, "E17.6.15.0", {"start": v(-3.1, -0.6) * mm, "end": v(-2.8, -0.55) * mm});
            skLineSegment(sketch, "E17.9.15.0", {"start": v(-2.84, -0.26) * mm, "end": v(-2.8, -0.55) * mm});
            skLineSegment(sketch, "E17.2.16.0", {"start": v(-3.08, -0.66) * mm, "end": v(-2.8, -0.58) * mm});
            skLineSegment(sketch, "E17.3.16.0", {"start": v(-3.08, -0.66) * mm, "end": v(-3, -0.95) * mm});
            skLineSegment(sketch, "E17.6.16.0", {"start": v(-3, -0.95) * mm, "end": v(-2.72, -0.87) * mm});
            skLineSegment(sketch, "E17.9.16.0", {"start": v(-2.8, -0.58) * mm, "end": v(-2.72, -0.87) * mm});
            skLineSegment(sketch, "E17.2.17.0", {"start": v(-2.99, -1) * mm, "end": v(-2.71, -0.9) * mm});
            skLineSegment(sketch, "E17.3.17.0", {"start": v(-2.99, -1) * mm, "end": v(-2.88, -1.28) * mm});
            skLineSegment(sketch, "E17.6.17.0", {"start": v(-2.88, -1.28) * mm, "end": v(-2.6, -1.17) * mm});
            skLineSegment(sketch, "E17.9.17.0", {"start": v(-2.71, -0.9) * mm, "end": v(-2.6, -1.17) * mm});
            skLineSegment(sketch, "E17.2.18.0", {"start": v(-2.86, -1.34) * mm, "end": v(-2.6, -1.2) * mm});
            skLineSegment(sketch, "E17.3.18.0", {"start": v(-2.86, -1.34) * mm, "end": v(-2.72, -1.6) * mm});
            skLineSegment(sketch, "E17.6.18.0", {"start": v(-2.72, -1.6) * mm, "end": v(-2.45, -1.46) * mm});
            skLineSegment(sketch, "E17.9.18.0", {"start": v(-2.6, -1.2) * mm, "end": v(-2.45, -1.46) * mm});
            skLineSegment(sketch, "E17.2.19.0", {"start": v(-2.68, -1.65) * mm, "end": v(-2.44, -1.48) * mm});
            skLineSegment(sketch, "E17.3.19.0", {"start": v(-2.68, -1.65) * mm, "end": v(-2.52, -1.9) * mm});
            skLineSegment(sketch, "E17.6.19.0", {"start": v(-2.52, -1.9) * mm, "end": v(-2.27, -1.73) * mm});
            skLineSegment(sketch, "E17.9.19.0", {"start": v(-2.44, -1.48) * mm, "end": v(-2.27, -1.73) * mm});
            skLineSegment(sketch, "E18.2.20.0", {"start": v(-2.48, -1.95) * mm, "end": v(-2.25, -1.75) * mm});
            skLineSegment(sketch, "E18.3.20.0", {"start": v(-2.48, -1.95) * mm, "end": v(-2.28, -2.18) * mm});
            skLineSegment(sketch, "E18.6.20.0", {"start": v(-2.28, -2.18) * mm, "end": v(-2.06, -1.98) * mm});
            skLineSegment(sketch, "E18.9.20.0", {"start": v(-2.25, -1.75) * mm, "end": v(-2.06, -1.98) * mm});
            skLineSegment(sketch, "E18.2.21.0", {"start": v(-2.24, -2.22) * mm, "end": v(-2.04, -2) * mm});
            skLineSegment(sketch, "E18.3.21.0", {"start": v(-2.24, -2.22) * mm, "end": v(-2.02, -2.42) * mm});
            skLineSegment(sketch, "E18.6.21.0", {"start": v(-2.02, -2.42) * mm, "end": v(-1.82, -2.2) * mm});
            skLineSegment(sketch, "E18.9.21.0", {"start": v(-2.04, -2) * mm, "end": v(-1.82, -2.2) * mm});
            skLineSegment(sketch, "E18.2.22.0", {"start": v(-1.97, -2.46) * mm, "end": v(-1.8, -2.22) * mm});
            skLineSegment(sketch, "E18.3.22.0", {"start": v(-1.97, -2.46) * mm, "end": v(-1.73, -2.64) * mm});
            skLineSegment(sketch, "E18.6.22.0", {"start": v(-1.73, -2.64) * mm, "end": v(-1.55, -2.4) * mm});
            skLineSegment(sketch, "E18.9.22.0", {"start": v(-1.8, -2.22) * mm, "end": v(-1.55, -2.4) * mm});
            skLineSegment(sketch, "E18.2.23.0", {"start": v(-1.68, -2.67) * mm, "end": v(-1.53, -2.4) * mm});
            skLineSegment(sketch, "E18.3.23.0", {"start": v(-1.68, -2.67) * mm, "end": v(-1.42, -2.82) * mm});
            skLineSegment(sketch, "E18.6.23.0", {"start": v(-1.42, -2.82) * mm, "end": v(-1.27, -2.56) * mm});
            skLineSegment(sketch, "E18.9.23.0", {"start": v(-1.53, -2.4) * mm, "end": v(-1.27, -2.56) * mm});
            skLineSegment(sketch, "E18.2.24.0", {"start": v(-1.36, -2.84) * mm, "end": v(-1.25, -2.57) * mm});
            skLineSegment(sketch, "E18.3.24.0", {"start": v(-1.36, -2.84) * mm, "end": v(-1.09, -2.96) * mm});
            skLineSegment(sketch, "E18.6.24.0", {"start": v(-1.09, -2.96) * mm, "end": v(-0.97, -2.68) * mm});
            skLineSegment(sketch, "E18.9.24.0", {"start": v(-1.25, -2.57) * mm, "end": v(-0.97, -2.68) * mm});
            skLineSegment(sketch, "E18.2.25.0", {"start": v(-1.03, -2.98) * mm, "end": v(-0.95, -2.7) * mm});
            skLineSegment(sketch, "E18.3.25.0", {"start": v(-1.03, -2.98) * mm, "end": v(-0.74, -3.06) * mm});
            skLineSegment(sketch, "E18.6.25.0", {"start": v(-0.74, -3.06) * mm, "end": v(-0.66, -2.78) * mm});
            skLineSegment(sketch, "E18.9.25.0", {"start": v(-0.95, -2.7) * mm, "end": v(-0.66, -2.78) * mm});
            skLineSegment(sketch, "E18.2.26.0", {"start": v(-0.68, -3.08) * mm, "end": v(-0.63, -2.78) * mm});
            skLineSegment(sketch, "E18.3.26.0", {"start": v(-0.68, -3.08) * mm, "end": v(-0.39, -3.13) * mm});
            skLineSegment(sketch, "E18.6.26.0", {"start": v(-0.39, -3.13) * mm, "end": v(-0.34, -2.83) * mm});
            skLineSegment(sketch, "E18.9.26.0", {"start": v(-0.63, -2.78) * mm, "end": v(-0.34, -2.83) * mm});
            skLineSegment(sketch, "E18.2.27.0", {"start": v(-0.33, -3.14) * mm, "end": v(-0.31, -2.84) * mm});
            skLineSegment(sketch, "E18.3.27.0", {"start": v(-0.33, -3.14) * mm, "end": v(-0.03, -3.15) * mm});
            skLineSegment(sketch, "E18.6.27.0", {"start": v(-0.03, -3.15) * mm, "end": v(-0.01, -2.85) * mm});
            skLineSegment(sketch, "E18.9.27.0", {"start": v(-0.31, -2.84) * mm, "end": v(-0.01, -2.85) * mm});
            skLineSegment(sketch, "E18.2.28.0", {"start": v(0.03, -3.15) * mm, "end": v(0.01, -2.85) * mm});
            skLineSegment(sketch, "E18.3.28.0", {"start": v(0.03, -3.15) * mm, "end": v(0.33, -3.14) * mm});
            skLineSegment(sketch, "E18.6.28.0", {"start": v(0.33, -3.14) * mm, "end": v(0.31, -2.84) * mm});
            skLineSegment(sketch, "E18.9.28.0", {"start": v(0.01, -2.85) * mm, "end": v(0.31, -2.84) * mm});
            skLineSegment(sketch, "E18.2.29.0", {"start": v(0.39, -3.13) * mm, "end": v(0.34, -2.83) * mm});
            skLineSegment(sketch, "E18.3.29.0", {"start": v(0.39, -3.13) * mm, "end": v(0.68, -3.08) * mm});
            skLineSegment(sketch, "E18.6.29.0", {"start": v(0.68, -3.08) * mm, "end": v(0.63, -2.78) * mm});
            skLineSegment(sketch, "E18.9.29.0", {"start": v(0.34, -2.83) * mm, "end": v(0.63, -2.78) * mm});
            skLineSegment(sketch, "E19.2.30.0", {"start": v(0.74, -3.06) * mm, "end": v(0.66, -2.78) * mm});
            skLineSegment(sketch, "E19.3.30.0", {"start": v(0.74, -3.06) * mm, "end": v(1.03, -2.98) * mm});
            skLineSegment(sketch, "E19.6.30.0", {"start": v(1.03, -2.98) * mm, "end": v(0.95, -2.7) * mm});
            skLineSegment(sketch, "E19.9.30.0", {"start": v(0.66, -2.78) * mm, "end": v(0.95, -2.7) * mm});
            skLineSegment(sketch, "E19.2.31.0", {"start": v(1.09, -2.96) * mm, "end": v(0.97, -2.68) * mm});
            skLineSegment(sketch, "E19.3.31.0", {"start": v(1.09, -2.96) * mm, "end": v(1.36, -2.84) * mm});
            skLineSegment(sketch, "E19.6.31.0", {"start": v(1.36, -2.84) * mm, "end": v(1.25, -2.57) * mm});
            skLineSegment(sketch, "E19.9.31.0", {"start": v(0.97, -2.68) * mm, "end": v(1.25, -2.57) * mm});
            skLineSegment(sketch, "E19.2.32.0", {"start": v(1.42, -2.82) * mm, "end": v(1.27, -2.56) * mm});
            skLineSegment(sketch, "E19.3.32.0", {"start": v(1.42, -2.82) * mm, "end": v(1.68, -2.67) * mm});
            skLineSegment(sketch, "E19.6.32.0", {"start": v(1.68, -2.67) * mm, "end": v(1.53, -2.4) * mm});
            skLineSegment(sketch, "E19.9.32.0", {"start": v(1.27, -2.56) * mm, "end": v(1.53, -2.4) * mm});
            skLineSegment(sketch, "E19.2.33.0", {"start": v(1.73, -2.64) * mm, "end": v(1.55, -2.4) * mm});
            skLineSegment(sketch, "E19.3.33.0", {"start": v(1.73, -2.64) * mm, "end": v(1.97, -2.46) * mm});
            skLineSegment(sketch, "E19.6.33.0", {"start": v(1.97, -2.46) * mm, "end": v(1.8, -2.22) * mm});
            skLineSegment(sketch, "E19.9.33.0", {"start": v(1.55, -2.4) * mm, "end": v(1.8, -2.22) * mm});
            skLineSegment(sketch, "E19.2.34.0", {"start": v(2.02, -2.42) * mm, "end": v(1.82, -2.2) * mm});
            skLineSegment(sketch, "E19.3.34.0", {"start": v(2.02, -2.42) * mm, "end": v(2.24, -2.22) * mm});
            skLineSegment(sketch, "E19.6.34.0", {"start": v(2.24, -2.22) * mm, "end": v(2.04, -2) * mm});
            skLineSegment(sketch, "E19.9.34.0", {"start": v(1.82, -2.2) * mm, "end": v(2.04, -2) * mm});
            skLineSegment(sketch, "E19.2.35.0", {"start": v(2.28, -2.18) * mm, "end": v(2.06, -1.98) * mm});
            skLineSegment(sketch, "E19.3.35.0", {"start": v(2.28, -2.18) * mm, "end": v(2.48, -1.95) * mm});
            skLineSegment(sketch, "E19.6.35.0", {"start": v(2.48, -1.95) * mm, "end": v(2.25, -1.75) * mm});
            skLineSegment(sketch, "E19.9.35.0", {"start": v(2.06, -1.98) * mm, "end": v(2.25, -1.75) * mm});
            skLineSegment(sketch, "E19.2.36.0", {"start": v(2.52, -1.9) * mm, "end": v(2.27, -1.73) * mm});
            skLineSegment(sketch, "E19.3.36.0", {"start": v(2.52, -1.9) * mm, "end": v(2.68, -1.65) * mm});
            skLineSegment(sketch, "E19.6.36.0", {"start": v(2.68, -1.65) * mm, "end": v(2.44, -1.48) * mm});
            skLineSegment(sketch, "E19.9.36.0", {"start": v(2.27, -1.73) * mm, "end": v(2.44, -1.48) * mm});
            skLineSegment(sketch, "E19.2.37.0", {"start": v(2.72, -1.6) * mm, "end": v(2.45, -1.46) * mm});
            skLineSegment(sketch, "E19.3.37.0", {"start": v(2.72, -1.6) * mm, "end": v(2.86, -1.34) * mm});
            skLineSegment(sketch, "E19.6.37.0", {"start": v(2.86, -1.34) * mm, "end": v(2.6, -1.2) * mm});
            skLineSegment(sketch, "E19.9.37.0", {"start": v(2.45, -1.46) * mm, "end": v(2.6, -1.2) * mm});
            skLineSegment(sketch, "E19.2.38.0", {"start": v(2.88, -1.28) * mm, "end": v(2.6, -1.17) * mm});
            skLineSegment(sketch, "E19.3.38.0", {"start": v(2.88, -1.28) * mm, "end": v(2.99, -1) * mm});
            skLineSegment(sketch, "E19.6.38.0", {"start": v(2.99, -1) * mm, "end": v(2.71, -0.9) * mm});
            skLineSegment(sketch, "E19.9.38.0", {"start": v(2.6, -1.17) * mm, "end": v(2.71, -0.9) * mm});
            skLineSegment(sketch, "E19.2.39.0", {"start": v(3, -0.95) * mm, "end": v(2.72, -0.87) * mm});
            skLineSegment(sketch, "E19.3.39.0", {"start": v(3, -0.95) * mm, "end": v(3.08, -0.66) * mm});
            skLineSegment(sketch, "E19.6.39.0", {"start": v(3.08, -0.66) * mm, "end": v(2.8, -0.58) * mm});
            skLineSegment(sketch, "E19.9.39.0", {"start": v(2.72, -0.87) * mm, "end": v(2.8, -0.58) * mm});
            skLineSegment(sketch, "E20.2.40.0", {"start": v(3.1, -0.6) * mm, "end": v(2.8, -0.55) * mm});
            skLineSegment(sketch, "E20.3.40.0", {"start": v(3.1, -0.6) * mm, "end": v(3.14, -0.3) * mm});
            skLineSegment(sketch, "E20.6.40.0", {"start": v(3.14, -0.3) * mm, "end": v(2.84, -0.26) * mm});
            skLineSegment(sketch, "E20.9.40.0", {"start": v(2.8, -0.55) * mm, "end": v(2.84, -0.26) * mm});
            skLineSegment(sketch, "E20.2.41.0", {"start": v(3.14, -0.24) * mm, "end": v(2.84, -0.23) * mm});
            skLineSegment(sketch, "E20.3.41.0", {"start": v(3.14, -0.24) * mm, "end": v(3.15, 0.06) * mm});
            skLineSegment(sketch, "E20.6.41.0", {"start": v(3.15, 0.06) * mm, "end": v(2.85, 0.07) * mm});
            skLineSegment(sketch, "E20.9.41.0", {"start": v(2.84, -0.23) * mm, "end": v(2.85, 0.07) * mm});
            skLineSegment(sketch, "E20.2.42.0", {"start": v(3.15, 0.12) * mm, "end": v(2.85, 0.1) * mm});
            skLineSegment(sketch, "E20.3.42.0", {"start": v(3.15, 0.12) * mm, "end": v(3.13, 0.42) * mm});
            skLineSegment(sketch, "E20.6.42.0", {"start": v(3.13, 0.42) * mm, "end": v(2.83, 0.4) * mm});
            skLineSegment(sketch, "E20.9.42.0", {"start": v(2.85, 0.1) * mm, "end": v(2.83, 0.4) * mm});
            skLineSegment(sketch, "E20.2.43.0", {"start": v(3.12, 0.48) * mm, "end": v(2.82, 0.42) * mm});
            skLineSegment(sketch, "E20.3.43.0", {"start": v(3.12, 0.48) * mm, "end": v(3.06, 0.77) * mm});
            skLineSegment(sketch, "E20.6.43.0", {"start": v(3.06, 0.77) * mm, "end": v(2.76, 0.71) * mm});
            skLineSegment(sketch, "E20.9.43.0", {"start": v(2.82, 0.42) * mm, "end": v(2.76, 0.71) * mm});
            skLineSegment(sketch, "E20.2.44.0", {"start": v(3.04, 0.83) * mm, "end": v(2.76, 0.74) * mm});
            skLineSegment(sketch, "E20.3.44.0", {"start": v(3.04, 0.83) * mm, "end": v(2.95, 1.12) * mm});
            skLineSegment(sketch, "E20.6.44.0", {"start": v(2.95, 1.12) * mm, "end": v(2.66, 1.02) * mm});
            skLineSegment(sketch, "E20.9.44.0", {"start": v(2.76, 0.74) * mm, "end": v(2.66, 1.02) * mm});
            skLineSegment(sketch, "E20.2.45.0", {"start": v(2.93, 1.17) * mm, "end": v(2.65, 1.05) * mm});
            skLineSegment(sketch, "E20.3.45.0", {"start": v(2.93, 1.17) * mm, "end": v(2.8, 1.45) * mm});
            skLineSegment(sketch, "E20.6.45.0", {"start": v(2.8, 1.45) * mm, "end": v(2.53, 1.32) * mm});
            skLineSegment(sketch, "E20.9.45.0", {"start": v(2.65, 1.05) * mm, "end": v(2.53, 1.32) * mm});
            skLineSegment(sketch, "E20.2.46.0", {"start": v(2.77, 1.5) * mm, "end": v(2.52, 1.34) * mm});
            skLineSegment(sketch, "E20.3.46.0", {"start": v(2.77, 1.5) * mm, "end": v(2.62, 1.76) * mm});
            skLineSegment(sketch, "E20.6.46.0", {"start": v(2.62, 1.76) * mm, "end": v(2.36, 1.6) * mm});
            skLineSegment(sketch, "E20.9.46.0", {"start": v(2.52, 1.34) * mm, "end": v(2.36, 1.6) * mm});
            skLineSegment(sketch, "E20.2.47.0", {"start": v(2.59, 1.8) * mm, "end": v(2.35, 1.62) * mm});
            skLineSegment(sketch, "E20.3.47.0", {"start": v(2.59, 1.8) * mm, "end": v(2.4, 2.04) * mm});
            skLineSegment(sketch, "E20.6.47.0", {"start": v(2.4, 2.04) * mm, "end": v(2.17, 1.86) * mm});
            skLineSegment(sketch, "E20.9.47.0", {"start": v(2.35, 1.62) * mm, "end": v(2.17, 1.86) * mm});
            skLineSegment(sketch, "E20.2.48.0", {"start": v(2.36, 2.09) * mm, "end": v(2.15, 1.88) * mm});
            skLineSegment(sketch, "E20.3.48.0", {"start": v(2.36, 2.09) * mm, "end": v(2.15, 2.3) * mm});
            skLineSegment(sketch, "E20.6.48.0", {"start": v(2.15, 2.3) * mm, "end": v(1.94, 2.1) * mm});
            skLineSegment(sketch, "E20.9.48.0", {"start": v(2.15, 1.88) * mm, "end": v(1.94, 2.1) * mm});
            skLineSegment(sketch, "E20.2.49.0", {"start": v(2.11, 2.34) * mm, "end": v(1.92, 2.11) * mm});
            skLineSegment(sketch, "E20.3.49.0", {"start": v(2.11, 2.34) * mm, "end": v(1.88, 2.53) * mm});
            skLineSegment(sketch, "E20.6.49.0", {"start": v(1.88, 2.53) * mm, "end": v(1.69, 2.3) * mm});
            skLineSegment(sketch, "E20.9.49.0", {"start": v(1.92, 2.11) * mm, "end": v(1.69, 2.3) * mm});
            skLineSegment(sketch, "E21.2.50.0", {"start": v(1.83, 2.57) * mm, "end": v(1.67, 2.32) * mm});
            skLineSegment(sketch, "E21.3.50.0", {"start": v(1.83, 2.57) * mm, "end": v(1.58, 2.73) * mm});
            skLineSegment(sketch, "E21.6.50.0", {"start": v(1.58, 2.73) * mm, "end": v(1.41, 2.48) * mm});
            skLineSegment(sketch, "E21.9.50.0", {"start": v(1.67, 2.32) * mm, "end": v(1.41, 2.48) * mm});
            skLineSegment(sketch, "E21.2.51.0", {"start": v(1.52, 2.76) * mm, "end": v(1.4, 2.5) * mm});
            skLineSegment(sketch, "E21.3.51.0", {"start": v(1.52, 2.76) * mm, "end": v(1.26, 2.9) * mm});
            skLineSegment(sketch, "E21.6.51.0", {"start": v(1.26, 2.9) * mm, "end": v(1.12, 2.62) * mm});
            skLineSegment(sketch, "E21.9.51.0", {"start": v(1.4, 2.5) * mm, "end": v(1.12, 2.62) * mm});
            skLineSegment(sketch, "E21.2.52.0", {"start": v(1.2, 2.92) * mm, "end": v(1.1, 2.63) * mm});
            skLineSegment(sketch, "E21.3.52.0", {"start": v(1.2, 2.92) * mm, "end": v(0.92, 3.02) * mm});
            skLineSegment(sketch, "E21.6.52.0", {"start": v(0.92, 3.02) * mm, "end": v(0.82, 2.73) * mm});
            skLineSegment(sketch, "E21.9.52.0", {"start": v(1.1, 2.63) * mm, "end": v(0.82, 2.73) * mm});
            skLineSegment(sketch, "E21.2.53.0", {"start": v(0.86, 3.03) * mm, "end": v(0.8, 2.74) * mm});
            skLineSegment(sketch, "E21.3.53.0", {"start": v(0.86, 3.03) * mm, "end": v(0.57, 3.1) * mm});
            skLineSegment(sketch, "E21.6.53.0", {"start": v(0.57, 3.1) * mm, "end": v(0.5, 2.8) * mm});
            skLineSegment(sketch, "E21.9.53.0", {"start": v(0.8, 2.74) * mm, "end": v(0.5, 2.8) * mm});
            skLineSegment(sketch, "E21.2.54.0", {"start": v(0.5, 3.11) * mm, "end": v(0.47, 2.81) * mm});
            skLineSegment(sketch, "E21.3.54.0", {"start": v(0.5, 3.11) * mm, "end": v(0.21, 3.15) * mm});
            skLineSegment(sketch, "E21.6.54.0", {"start": v(0.21, 3.15) * mm, "end": v(0.18, 2.85) * mm});
            skLineSegment(sketch, "E21.9.54.0", {"start": v(0.47, 2.81) * mm, "end": v(0.18, 2.85) * mm});
            skSolve(sketch);
        }
        {
            var Q0;
            Q0=qSketchRegion(id+"F6",true);
            extrude(context, id + "F7", {"entities" : qUnion([Q0]), "operationType" : NewBodyOperationType.ADD, "oppositeDirection" : true, "depth" : 5 * mm});
        }
    });
